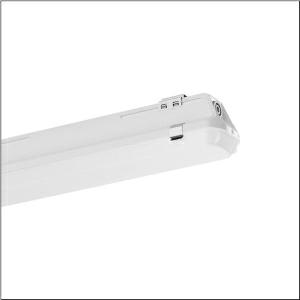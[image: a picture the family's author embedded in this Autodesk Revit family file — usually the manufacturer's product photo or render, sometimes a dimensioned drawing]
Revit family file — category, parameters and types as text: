
# Revit family: monsun_r__21_51fb107l440j_daa1
name_source: partatom
category: Lighting Fixtures
units: mm (PartAtom-declared; Revit-internal decimal feet)

## family parameters
Cut with Voids When Loaded = No
Host = Face
Light Source = No
Part Type = Normal
Room Calculation Point = No
Round Connector Dimension = Use Diameter
Shared = No

## types (1)
- Monsun® 21 (1 x LED, 4470 lm, 27.2 W, 4000K)
    Apparent Load = 27 VA
    CIE Flux Codes = 46 76 93 94 100
    Color Rendering = 80
    Color Temperature = 4000K
    Default Elevation = 1800 mm
    Description = Monsun® 21, damp-proof luminaire, chain hanger, primary optical cover: enclosure, of PMMA, light emission: direct distribution, primary light characteristic: symmetric, installation type: suspended mounting, surface-mounted, horizontal mounting, vertical mounting, LED, rated luminous flux: 4.470lm, luminous efficacy: 166lm/W, light colour: 840, colour temperature: 4000K, control gear: ECG, with terminal, 3-pole, max. 2.5mm², mains connection: 220..240V, AC, 50/60Hz, rated input power: 27W, housing, of glass-fibre reinforced plastic, uncoated, bright grey, incl. chain hanger, length: 1.299mm, width: 90mm, height: 88mm, clip for enclosure, of stainless steel (V2A), ceiling mounting element, of stainless steel (V2A), chain hanger, of stainless steel (V2A), protection rating (complete): IP66, insulation class (complete): insulation class I (protective earthing), certification: CE, ENEC, VDE, UKCA, protection symbol: D, impact resistance: IK04, permissible operating ambient temperature: -25..+35°C, standard: EN 50419, EN 60598-2-1, no direct snow, no direct sun, no direct rain, for indoor or canopied outdoor use, corresponds to IFS (International Featured Standards) requirements for safety and quality in the food industry, contact your sales advisor before using the luminaires in applications with unclear chemical exposure, large temperature fluctuations or condensation-forming humidity, LABS conformity tested according to VDMA 24364:2018-05, packaging unit: 1 piece
    Height = 88 mm
    Lamp = 1 x LED
    Lamp Light Flux = 4470 lm
    Lamp Power = 27.2 W
    Lamp count = 1
    Length = 1299 mm
    Luminous efficacy = 164 lm/W
    Manufacturer = Siteco
    ModVariant = No
    Model = 51FB107L440J
    Mounting Place = Ceiling
    Mounting Type = Surface mounted
    Number of Poles = 1
    OnlyDefault = Yes
    Power Factor = 1
    Product Name = Monsun® 21
    Product group = damp-proof luminaire
    ProductGroupID = 300
    Protection Class = Protection class I
    Protection Degree = IP 66
    RLX_Detail_Level = 1
    RLX_Emergency_Light_Flux = 0 lm
    RLX_Emergency_Type = 0
    RLX_Emergency_Type_DB = No
    RlxData = <blob elided: 89525 chars, md5=91fbb424>
    Socket = socket
    Standby Power = 0 W
    System Light Flux = 4470 lm
    System Power = 27 W
    Type Comments = Product without accessories
    Type Image = l_1006717.jpg
    URL = http://relux.com
    VarID = ---
    Voltage = 0 V
    Weight = 0.00 kg
    Width = 90 mm

## geometry (parser evidence)
native form markers: Blend x4, Sweep x13
no freeform markers — native parametric forms only
